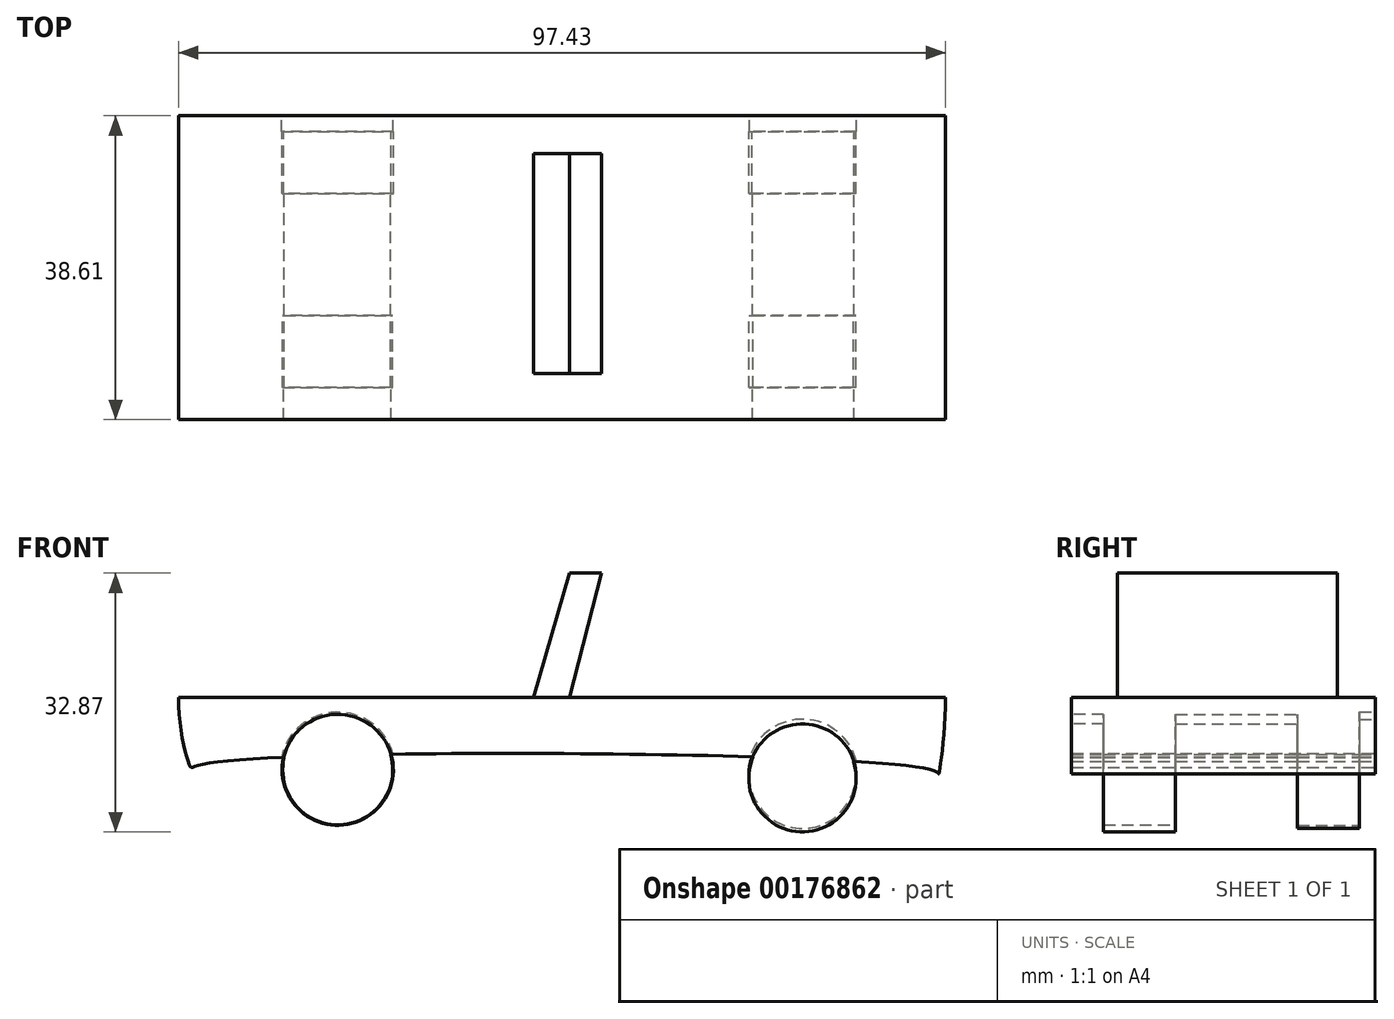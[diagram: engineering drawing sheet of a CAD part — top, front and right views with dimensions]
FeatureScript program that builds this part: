
annotation { "Feature Type Name" : "Feature", "Feature Type Description" : "" }
export const myFeature = defineFeature(function(context is Context, id is Id, definition is map)
    precondition{}
    {
        {
            var Q0;
            Q0=qCreatedBy(makeId("Front.planeOp"),FACE);
            var sketch = newSketch(context, id + "F0", { "sketchPlane" : qUnion([Q0])});
            skFitSpline(sketch, "E0", {"points": [v(-50.97, -8.66) * mm, v(-50.97, 5.55) * mm, v(-20.51, 5.14) * mm, v(17.13, 4.2) * mm, v(43.39, 8.12) * mm, v(44.2, -9.75) * mm, v(43.93, -9.48) * mm, v(-49.35, -8.53) * mm, v(-50.97, -8.66) * mm]});
            skLineSegment(sketch, "E1", {"start": v(-20.51, 5.14) * mm, "end": v(-15.64, 12.86) * mm});
            skLineSegment(sketch, "E2", {"start": v(-15.64, 12.86) * mm, "end": v(-10.63, 12.86) * mm});
            skLineSegment(sketch, "E3", {"start": v(-10.63, 12.86) * mm, "end": v(-10.63, 3.26) * mm});
            skLineSegment(sketch, "E4", {"start": v(-10.63, 3.26) * mm, "end": v(-10.63, 12.86) * mm});
            skLineSegment(sketch, "E5", {"start": v(5.35, 12.86) * mm, "end": v(5.35, 2.25) * mm});
            skLineSegment(sketch, "E6", {"start": v(-10.63, 12.86) * mm, "end": v(5.35, 12.86) * mm});
            skLineSegment(sketch, "E7", {"start": v(5.35, 12.86) * mm, "end": v(9.27, 12.86) * mm});
            skLineSegment(sketch, "E8", {"start": v(9.27, 12.86) * mm, "end": v(17.13, 4.2) * mm});
            skPoint(sketch, "E9.2.internal.snap0", {"position": v(7.31, 12.86) * mm});
            skFitSpline(sketch, "E9", {"points": [v(-15.64, 12.86) * mm, v(-14.42, 13.94) * mm, v(7.31, 13.94) * mm, v(9.27, 12.86) * mm, v(-15.64, 12.86) * mm]});
            skCircle(sketch, "E10", {"center": v(-32.15, -9.2) * mm, "radius": 6.99 * mm});
            skCircle(sketch, "E11", {"center": v(26.87, -10.29) * mm, "radius": 6.81 * mm});
            skSolve(sketch);
        }
        {
            var Q0;
            Q0 = qSketchRegion(id + "F0", true);
            extrude(context, id + "F1", {"entities" : qUnion([Q0]), "depth" : 38.6 * mm});
        }
        {
            var Q0;
            Q0=makeQuery(id+"F1.opExtrude","CAP_FACE",FACE,{"disambiguationData":[OSD([sQuery(id+"F0.wireOp",EDGE,"E0"),sQuery(id+"F0.wireOp",EDGE,"E1"),sQuery(id+"F0.wireOp",EDGE,"E4"),sQuery(id+"F0.wireOp",EDGE,"E5"),sQuery(id+"F0.wireOp",EDGE,"E6"),sQuery(id+"F0.wireOp",EDGE,"E8"),sQuery(id+"F0.wireOp",EDGE,"E9"),sQuery(id+"F0.wireOp",EDGE,"E10"),sQuery(id+"F0.wireOp",EDGE,"E11"),sQuery(id+"F0.wireOp",EDGE,"E0")])],"isStart":false});
            var sketch = newSketch(context, id + "F2", { "sketchPlane" : qUnion([Q0])});
            skCircle(sketch, "E12", {"center": v(-32.15, -9.2) * mm, "radius": 7.04 * mm});
            skCircle(sketch, "E13", {"center": v(26.87, -10.29) * mm, "radius": 6.9 * mm});
            skSolve(sketch);
        }
        {
            var Q0;
            Q0 = qSketchRegion(id + "F2", true);
            var Q1;
            {var subQ2=sQuery(id+"F0.wireOp",EDGE,"E10");var subQ7=makeQuery(id+"F1.opExtrude","CAP_EDGE",EDGE,{"disambiguationData":[OSD([subQ2])],"isStart":false});Q1=makeQuery(id+"F2.imprint","IMPRINT",FACE,{"disambiguationData":[TD([[makeQuery(id+"F2.imprint","IMPRINT",EDGE,{"derivedFrom":subQ7}),1.0]])]});}
            extrude(context, id + "F3", {"entities" : qUnion([Q0, Q1]), "operationType" : NewBodyOperationType.REMOVE, "oppositeDirection" : true, "depth" : 4.06 * mm});
        }
        {
            var Q0;
            Q0=makeQuery(id+"F1.opExtrude","CAP_FACE",FACE,{"disambiguationData":[OSD([sQuery(id+"F0.wireOp",EDGE,"E0"),sQuery(id+"F0.wireOp",EDGE,"E1"),sQuery(id+"F0.wireOp",EDGE,"E4"),sQuery(id+"F0.wireOp",EDGE,"E5"),sQuery(id+"F0.wireOp",EDGE,"E6"),sQuery(id+"F0.wireOp",EDGE,"E8"),sQuery(id+"F0.wireOp",EDGE,"E9"),sQuery(id+"F0.wireOp",EDGE,"E10"),sQuery(id+"F0.wireOp",EDGE,"E11"),sQuery(id+"F0.wireOp",EDGE,"E0")])],"isStart":true});
            var sketch = newSketch(context, id + "F4", { "sketchPlane" : qUnion([Q0])});
            skCircle(sketch, "E14", {"center": v(-26.87, -10.29) * mm, "radius": 6.9 * mm});
            skCircle(sketch, "E15", {"center": v(32.15, -9.2) * mm, "radius": 7 * mm});
            skSolve(sketch);
        }
        {
            var Q0;
            Q0 = qSketchRegion(id + "F4", true);
            extrude(context, id + "F5", {"entities" : qUnion([Q0]), "operationType" : NewBodyOperationType.REMOVE, "oppositeDirection" : true, "depth" : 25.4 * mm});
        }
        {
            var Q0;
            Q0=qCreatedBy(makeId("Front.planeOp"),FACE);
            var sketch = newSketch(context, id + "F6", { "sketchPlane" : qUnion([Q0])});
            skCircle(sketch, "E16", {"center": v(26.87, -9.88) * mm, "radius": 6.8 * mm});
            skCircle(sketch, "E17", {"center": v(-32.15, -9.2) * mm, "radius": 7.07 * mm});
            skSolve(sketch);
        }
        {
            var Q0;
            Q0=makeQuery(id+"F6.imprint","IMPRINT",FACE,{"disambiguationData":[TD([[makeQuery(id+"F6.imprint","IMPRINT",EDGE,{"derivedFrom":sQuery(id+"F6.wireOp",EDGE,"E16")}),1.0]])]});
            var Q1;
            Q1=makeQuery(id+"F6.imprint","IMPRINT",FACE,{"disambiguationData":[TD([[makeQuery(id+"F6.imprint","IMPRINT",EDGE,{"derivedFrom":sQuery(id+"F6.wireOp",EDGE,"E17")}),1.0]])]});
            extrude(context, id + "F7", {"entities" : qUnion([Q0, Q1]), "operationType" : NewBodyOperationType.ADD, "depth" : 9.9 * mm});
        }
        {
            var Q0;
            Q0=makeQuery(id+"F7.boolean.opBoolean","MERGE",FACE,{"derivedFrom":[makeQuery(id+"F1.opExtrude","CAP_FACE",FACE,{"disambiguationData":[OSD([sQuery(id+"F0.wireOp",EDGE,"E0"),sQuery(id+"F0.wireOp",EDGE,"E1"),sQuery(id+"F0.wireOp",EDGE,"E4"),sQuery(id+"F0.wireOp",EDGE,"E5"),sQuery(id+"F0.wireOp",EDGE,"E6"),sQuery(id+"F0.wireOp",EDGE,"E8"),sQuery(id+"F0.wireOp",EDGE,"E9"),sQuery(id+"F0.wireOp",EDGE,"E10"),sQuery(id+"F0.wireOp",EDGE,"E11"),sQuery(id+"F0.wireOp",EDGE,"E0")])],"isStart":true}),makeQuery(id+"F7.opExtrude","CAP_FACE",FACE,{"disambiguationData":[OSD([sQuery(id+"F6.wireOp",EDGE,"E16")])],"isStart":true}),makeQuery(id+"F7.opExtrude","CAP_FACE",FACE,{"disambiguationData":[OSD([sQuery(id+"F6.wireOp",EDGE,"E17")])],"isStart":true})]});
            var sketch = newSketch(context, id + "F8", { "sketchPlane" : qUnion([Q0])});
            skCircle(sketch, "E18", {"center": v(-26.87, -9.88) * mm, "radius": 7.08 * mm});
            skCircle(sketch, "E19", {"center": v(32.15, -9.2) * mm, "radius": 7.32 * mm});
            skSolve(sketch);
        }
        {
            var Q0;
            Q0 = qSketchRegion(id + "F8", true);
            extrude(context, id + "F9", {"entities" : qUnion([Q0]), "operationType" : NewBodyOperationType.REMOVE, "oppositeDirection" : true, "depth" : 2.03 * mm});
        }
        {
            var Q0;
            Q0=qCreatedBy(makeId("Top.planeOp"),FACE);
            var sketch = newSketch(context, id + "F10", { "sketchPlane" : qUnion([Q0])});
            skLineSegment(sketch, "E20.bottom", {"start": v(-57.17, 0) * mm, "end": v(53.21, 0) * mm});
            skLineSegment(sketch, "E20.top", {"start": v(-57.17, -64.06) * mm, "end": v(53.21, -64.06) * mm});
            skLineSegment(sketch, "E20.left", {"start": v(-57.17, 0) * mm, "end": v(-57.17, -64.06) * mm});
            skLineSegment(sketch, "E20.right", {"start": v(53.21, 0) * mm, "end": v(53.21, -64.06) * mm});
            skSolve(sketch);
        }
        {
            var Q0;
            Q0 = qSketchRegion(id + "F10", true);
            extrude(context, id + "F11", {"entities" : qUnion([Q0]), "operationType" : NewBodyOperationType.REMOVE, "depth" : 38.35 * mm});
        }
        {
            var Q0;
            Q0=qCreatedBy(makeId("Front.planeOp"),FACE);
            var sketch = newSketch(context, id + "F12", { "sketchPlane" : qUnion([Q0])});
            skLineSegment(sketch, "E21", {"start": v(-7.27, 0) * mm, "end": v(-2.68, 15.77) * mm});
            skLineSegment(sketch, "E22", {"start": v(-2.68, 15.77) * mm, "end": v(1.37, 15.77) * mm});
            skLineSegment(sketch, "E23", {"start": v(1.37, 15.77) * mm, "end": v(-2.68, 0) * mm});
            skLineSegment(sketch, "E24", {"start": v(-7.27, 0) * mm, "end": v(-2.68, 0) * mm});
            skSolve(sketch);
        }
        {
            var Q0;
            Q0 = qSketchRegion(id + "F12", true);
            extrude(context, id + "F13", {"entities" : qUnion([Q0]), "operationType" : NewBodyOperationType.ADD, "depth" : 32.77 * mm});
        }
        {
            var Q0;
            Q0 = qSketchRegion(id + "F12", true);
            extrude(context, id + "F14", {"entities" : qUnion([Q0]), "operationType" : NewBodyOperationType.REMOVE, "depth" : 4.83 * mm});
        }
    });
